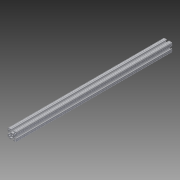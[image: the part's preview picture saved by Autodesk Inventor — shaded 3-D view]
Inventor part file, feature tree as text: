
AUTODESK INVENTOR PART (.ipt)
format: ipt  version: 2013 (Build 170138000, 138)  size: 288,768 bytes
history: native  units: in
note: dims shown in document units (in); Inventor stores cm internally (conversion verified against a paired STEP export)
features: extrude x1, sketch x1
ambient origin geometry x8: Origin, YZ Plane, XZ Plane, XY Plane, X Axis, Y Axis, Z Axis, Center Point
bodies: Solid1 (feature_tree)
feature tree (2):
  extrude  "Extrusion1"  [1 undecoded]
  sketch  "Sketch1"  dims[d0=27.0in d1=0.0in]
note: 1 required parameter value undecoded (feature->parameter linkage not recoverable at this tier; creation-order binding heuristic only, values carry confidence <= 0.55)
